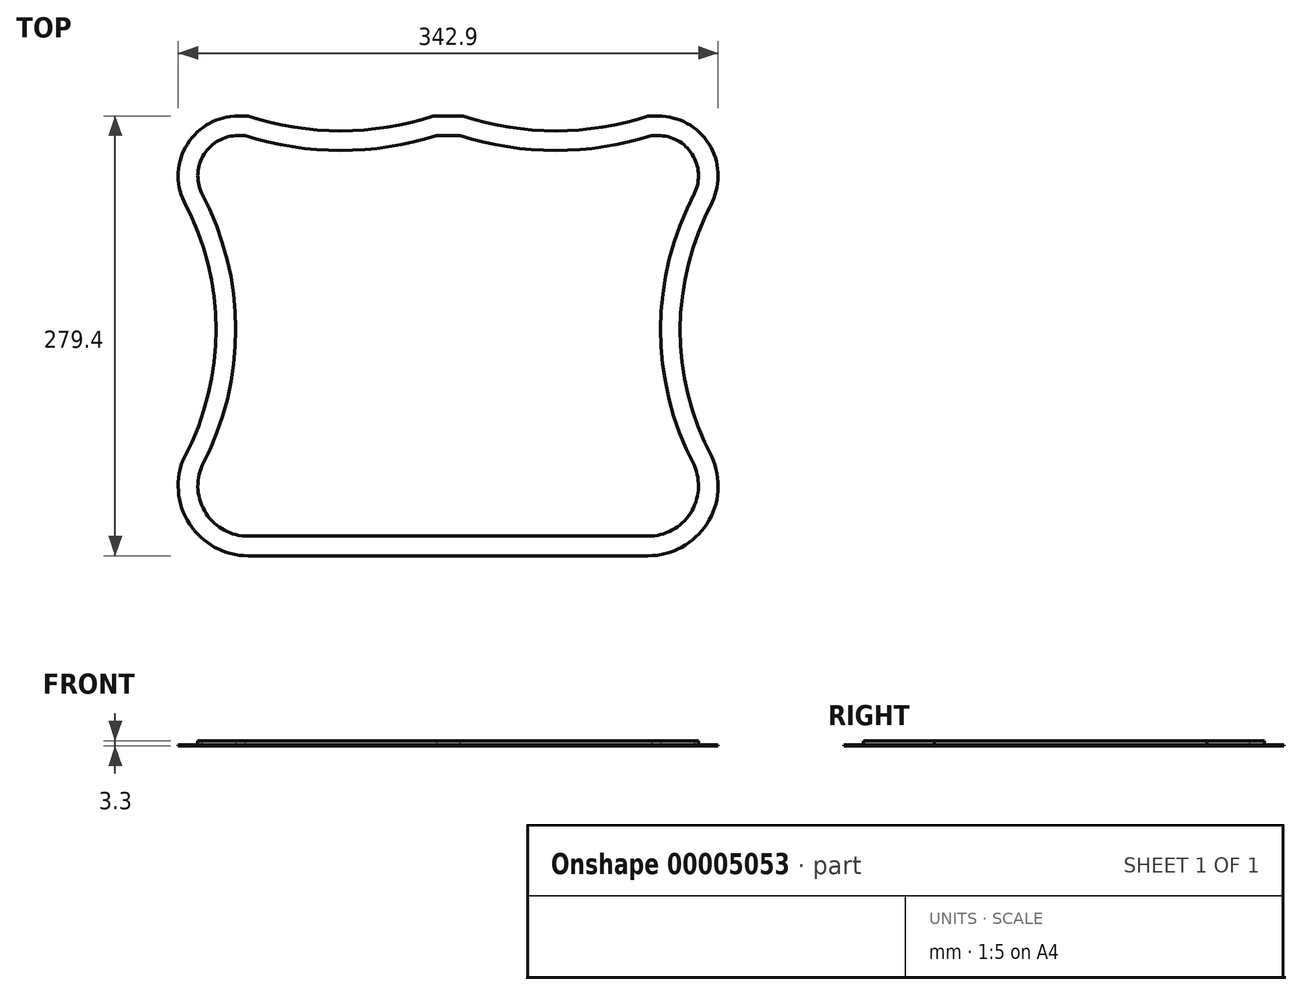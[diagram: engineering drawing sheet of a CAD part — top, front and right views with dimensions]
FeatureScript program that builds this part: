
annotation { "Feature Type Name" : "Feature", "Feature Type Description" : "" }
export const myFeature = defineFeature(function(context is Context, id is Id, definition is map)
    precondition{}
    {
        {
            var Q0;
            Q0=qCreatedBy(makeId("Top.planeOp"),FACE);
            var sketch = newSketch(context, id + "F0", { "sketchPlane" : qUnion([Q0])});
            skArc(sketch, "E0", {"start": v(-406.26, -160.5) * mm, "mid": v(-403.12, -202.93) * mm, "end": v(-365.76, -223.29) * mm});
            skLineSegment(sketch, "E1", {"start": v(-365.76, -223.29) * mm, "end": v(-111.76, -223.29) * mm});
            skArc(sketch, "E2", {"start": v(-111.76, -223.29) * mm, "mid": v(-74.4, -202.93) * mm, "end": v(-71.27, -160.5) * mm});
            skArc(sketch, "E3", {"start": v(-71.27, -160.5) * mm, "mid": v(-91.38, -79.43) * mm, "end": v(-71.04, 1.59) * mm});
            skArc(sketch, "E4", {"start": v(-71.04, 1.59) * mm, "mid": v(-73.18, 38.33) * mm, "end": v(-105.41, 56.11) * mm});
            skLineSegment(sketch, "E5", {"start": v(-105.41, 56.11) * mm, "end": v(-111.76, 56.11) * mm});
            skArc(sketch, "E6", {"start": v(-111.76, 56.11) * mm, "mid": v(-170.5, 46.59) * mm, "end": v(-229.24, 56.11) * mm});
            skLineSegment(sketch, "E7", {"start": v(-229.24, 56.11) * mm, "end": v(-248.29, 56.11) * mm});
            skArc(sketch, "E8", {"start": v(-248.29, 56.11) * mm, "mid": v(-307.03, 46.59) * mm, "end": v(-365.76, 56.11) * mm});
            skLineSegment(sketch, "E9", {"start": v(-365.76, 56.11) * mm, "end": v(-372.11, 56.11) * mm});
            skArc(sketch, "E10", {"start": v(-372.11, 56.11) * mm, "mid": v(-404.34, 38.33) * mm, "end": v(-406.5, 1.59) * mm});
            skArc(sketch, "E11", {"start": v(-406.5, 1.59) * mm, "mid": v(-386.14, -79.43) * mm, "end": v(-406.26, -160.5) * mm});
            skLineSegment(sketch, "E12", {"start": v(-410.21, 18.01) * mm, "end": v(-410.21, -165.91) * mm, "construction": true});
            skLineSegment(sketch, "E13", {"start": v(-67.31, 18.01) * mm, "end": v(-67.31, -122.1) * mm, "construction": true});
            skLineSegment(sketch, "E14", {"start": v(-238.76, 56.11) * mm, "end": v(-238.76, -223.29) * mm, "construction": true});
            skSolve(sketch);
        }
        {
            var Q0;
            Q0=qSketchRegion(id+"F0",true);
            extrude(context, id + "F1", {"entities" : qUnion([Q0]), "oppositeDirection" : true, "depth" : 3.3 * mm});
        }
        {
            var Q0;
            Q0=sQuery(id+"F0.wireOp",EDGE,"E1");
            var Q1;
            Q1=sQuery(id+"F0.wireOp",VERTEX,"E1.start");
            cPlane(context, id + "F2", {"entities" : qUnion([Q0, Q1]), "cplaneType" : CPlaneType.LINE_POINT, "offset" : 152.4 * mm, "width" : 152.4 * mm, "height" : 152.4 * mm});
        }
        {
            var Q0;
            Q0=qCreatedBy(makeId("Top.planeOp"),FACE);
            var sketch = newSketch(context, id + "F3", { "sketchPlane" : qUnion([Q0])});
            skLineSegment(sketch, "E15", {"start": v(20.84, 19.51) * mm, "end": v(118.06, 19.51) * mm});
            skArc(sketch, "E16", {"start": v(118.06, 19.51) * mm, "mid": v(135.88, 27.54) * mm, "end": v(141.66, 46.21) * mm});
            skArc(sketch, "E17", {"start": v(141.66, 46.21) * mm, "mid": v(117.96, 84.13) * mm, "end": v(74.5, 94.7) * mm});
            skArc(sketch, "E18", {"start": v(3.73, 52.44) * mm, "mid": v(2.29, 30.78) * mm, "end": v(20.84, 19.51) * mm});
            skLineSegment(sketch, "E19", {"start": v(3.73, 52.44) * mm, "end": v(74.5, 94.7) * mm});
            skLineSegment(sketch, "E20", {"start": v(64.73, 53.45) * mm, "end": v(64.73, 19.51) * mm, "construction": true});
            skSolve(sketch);
        }
        {
            var Q0;
            Q0=sQuery(id+"F3.wireOp",EDGE,"E15");
            var Q1;
            Q1=sQuery(id+"F3.wireOp",VERTEX,"E20.end");
            cPlane(context, id + "F4", {"entities" : qUnion([Q0, Q1]), "cplaneType" : CPlaneType.LINE_POINT, "offset" : 152.4 * mm, "width" : 152.4 * mm, "height" : 152.4 * mm});
        }
        {
            var Q0;
            Q0=qCreatedBy(id+"F2.planeOp",FACE);
            var sketch = newSketch(context, id + "F5", { "sketchPlane" : qUnion([Q0])});
            skPoint(sketch, "E21.0", {"position": v(-223.29, 0) * mm});
            skPoint(sketch, "E22.start.orphan", {"position": v(-210.84, 0) * mm});
            skLineSegment(sketch, "E23", {"start": v(-210.84, -2.48) * mm, "end": v(-210.84, 0.75) * mm});
            skLineSegment(sketch, "E24", {"start": v(-210.84, 0.75) * mm, "end": v(-223.85, 0.75) * mm});
            skLineSegment(sketch, "E25", {"start": v(-223.85, 0.75) * mm, "end": v(-223.85, -2.48) * mm});
            skPoint(sketch, "E26.start.orphan", {"position": v(-223.29, -2.48) * mm});
            skLineSegment(sketch, "E27", {"start": v(-210.84, -2.48) * mm, "end": v(-223.85, -2.48) * mm});
            skSolve(sketch);
        }
        {
            var Q0;
            Q0=makeQuery(id+"F0.imprint","IMPRINT",FACE,{"disambiguationData":[TD([[makeQuery(id+"F0.imprint","IMPRINT",EDGE,{"derivedFrom":sQuery(id+"F0.wireOp",EDGE,"E0")}),1.0]])]});
            var sketch = newSketch(context, id + "F6", { "sketchPlane" : qUnion([Q0])});
            skLineSegment(sketch, "E28.0", {"start": v(-365.76, -223.29) * mm, "end": v(-111.76, -223.29) * mm});
            skArc(sketch, "E29.0", {"start": v(-111.76, -223.29) * mm, "mid": v(-74.4, -202.93) * mm, "end": v(-71.27, -160.5) * mm});
            skArc(sketch, "E30.0", {"start": v(-71.27, -160.5) * mm, "mid": v(-91.38, -79.43) * mm, "end": v(-71.04, 1.59) * mm});
            skArc(sketch, "E31.0", {"start": v(-71.04, 1.59) * mm, "mid": v(-73.18, 38.33) * mm, "end": v(-105.41, 56.11) * mm});
            skLineSegment(sketch, "E32.0", {"start": v(-105.41, 56.11) * mm, "end": v(-111.76, 56.11) * mm});
            skArc(sketch, "E33.0", {"start": v(-111.76, 56.11) * mm, "mid": v(-170.5, 46.59) * mm, "end": v(-229.24, 56.11) * mm});
            skLineSegment(sketch, "E34.0", {"start": v(-229.24, 56.11) * mm, "end": v(-248.29, 56.11) * mm});
            skArc(sketch, "E35.0", {"start": v(-248.29, 56.11) * mm, "mid": v(-307.03, 46.59) * mm, "end": v(-365.76, 56.11) * mm});
            skLineSegment(sketch, "E36.0", {"start": v(-365.76, 56.11) * mm, "end": v(-372.11, 56.11) * mm});
            skArc(sketch, "E37.0", {"start": v(-372.11, 56.11) * mm, "mid": v(-404.34, 38.33) * mm, "end": v(-406.5, 1.59) * mm});
            skArc(sketch, "E38.0", {"start": v(-406.5, 1.59) * mm, "mid": v(-386.14, -79.43) * mm, "end": v(-406.26, -160.5) * mm});
            skArc(sketch, "E39.0", {"start": v(-406.26, -160.5) * mm, "mid": v(-403.12, -202.93) * mm, "end": v(-365.76, -223.29) * mm});
            skSolve(sketch);
        }
        {
            var Q0;
            Q0=makeQuery(id+"F5.imprint","IMPRINT",FACE,{"disambiguationData":[TD([[makeQuery(id+"F5.imprint","IMPRINT",EDGE,{"derivedFrom":sQuery(id+"F5.wireOp",EDGE,"E23")}),1.0]])]});
            var Q1;
            Q1=sQuery(id+"F6.wireOp",EDGE,"E28.0");
            var Q2;
            Q2=sQuery(id+"F6.wireOp",EDGE,"E29.0");
            var Q3;
            Q3=sQuery(id+"F6.wireOp",EDGE,"E30.0");
            var Q4;
            Q4=sQuery(id+"F6.wireOp",EDGE,"E31.0");
            var Q5;
            Q5=sQuery(id+"F6.wireOp",EDGE,"E32.0");
            var Q6;
            Q6=sQuery(id+"F6.wireOp",EDGE,"E33.0");
            var Q7;
            Q7=sQuery(id+"F6.wireOp",EDGE,"E34.0");
            var Q8;
            Q8=sQuery(id+"F6.wireOp",EDGE,"E35.0");
            var Q9;
            Q9=sQuery(id+"F6.wireOp",EDGE,"E36.0");
            var Q10;
            Q10=sQuery(id+"F6.wireOp",EDGE,"E37.0");
            var Q11;
            Q11=sQuery(id+"F6.wireOp",EDGE,"E38.0");
            var Q12;
            Q12=sQuery(id+"F6.wireOp",EDGE,"E39.0");
            sweep(context, id + "F7", {"operationType" : NewBodyOperationType.REMOVE, "profiles" : qUnion([Q0]), "path" : qUnion([Q1, Q2, Q3, Q4, Q5, Q6, Q7, Q8, Q9, Q10, Q11, Q12])});
        }
    });
